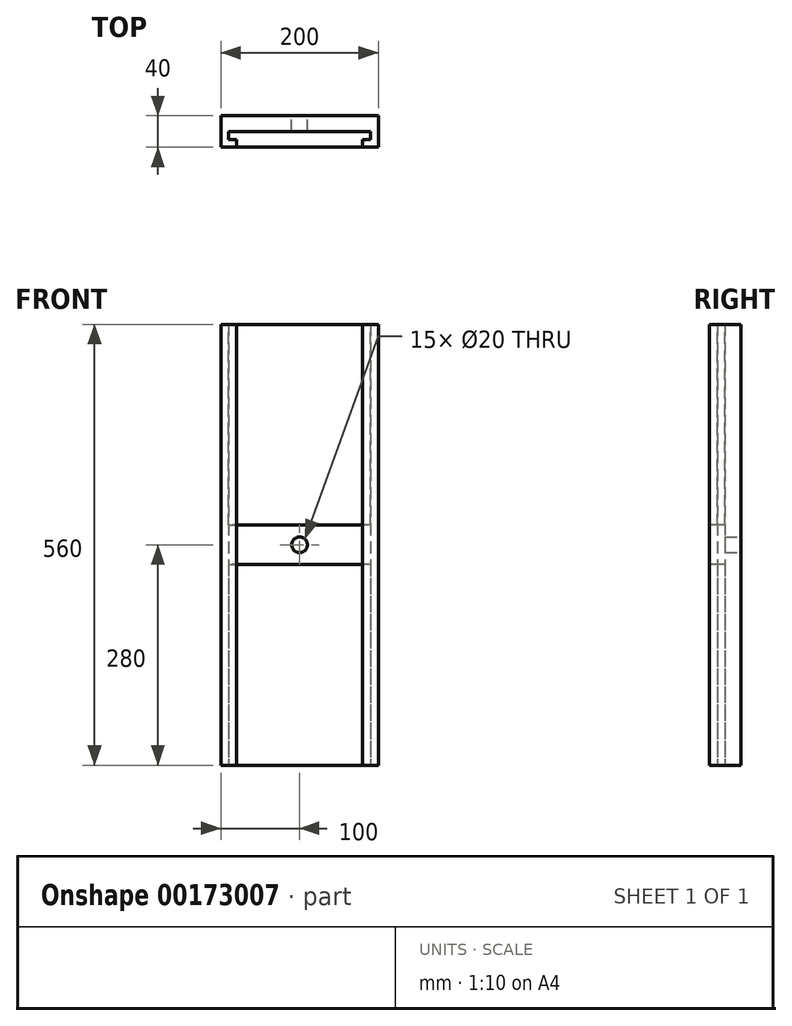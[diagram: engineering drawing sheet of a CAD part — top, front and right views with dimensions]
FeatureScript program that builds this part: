
annotation { "Feature Type Name" : "Feature", "Feature Type Description" : "" }
export const myFeature = defineFeature(function(context is Context, id is Id, definition is map)
    precondition{}
    {
        {
            var Q0;
            Q0=qCreatedBy(makeId("Top.planeOp"),FACE);
            var sketch = newSketch(context, id + "F0", { "sketchPlane" : qUnion([Q0])});
            skLineSegment(sketch, "E0", {"start": v(0, 20) * mm, "end": v(90, 20) * mm});
            skLineSegment(sketch, "E1", {"start": v(90, 20) * mm, "end": v(90, 10) * mm});
            skLineSegment(sketch, "E2", {"start": v(90, 10) * mm, "end": v(80, 10) * mm});
            skLineSegment(sketch, "E3", {"start": v(80, 10) * mm, "end": v(80, 0) * mm});
            skLineSegment(sketch, "E4", {"start": v(80, 0) * mm, "end": v(100, 0) * mm});
            skLineSegment(sketch, "E5", {"start": v(100, 0) * mm, "end": v(100, 40) * mm});
            skLineSegment(sketch, "E6", {"start": v(100, 40) * mm, "end": v(0, 40) * mm});
            skLineSegment(sketch, "E7", {"start": v(0, 40) * mm, "end": v(0, 0) * mm, "construction": true});
            skLineSegment(sketch, "E8.MirrorCS", {"start": v(-100, 40) * mm, "end": v(0, 40) * mm});
            skLineSegment(sketch, "E9.MirrorCS", {"start": v(0, 20) * mm, "end": v(-90, 20) * mm});
            skLineSegment(sketch, "E10.MirrorCS", {"start": v(-90, 20) * mm, "end": v(-90, 10) * mm});
            skLineSegment(sketch, "E11.MirrorCS", {"start": v(-90, 10) * mm, "end": v(-80, 10) * mm});
            skLineSegment(sketch, "E12.MirrorCS", {"start": v(-80, 10) * mm, "end": v(-80, 0) * mm});
            skLineSegment(sketch, "E13.MirrorCS", {"start": v(-80, 0) * mm, "end": v(-100, 0) * mm});
            skLineSegment(sketch, "E14.MirrorCS", {"start": v(-100, 0) * mm, "end": v(-100, 40) * mm});
            skSolve(sketch);
        }
        {
            var Q0;
            Q0 = qSketchRegion(id + "F0", true);
            extrude(context, id + "F1", {"entities" : qUnion([Q0]), "depth" : 280 * mm, "hasSecondDirection" : true, "secondDirectionOppositeDirection" : true, "secondDirectionDepth" : 280 * mm});
        }
        {
            var Q0;
            Q0=makeQuery(id+"F1.opExtrude","SWEPT_FACE",FACE,{"disambiguationData":[OSD([sQuery(id+"F0.wireOp",EDGE,"E6"),sQuery(id+"F0.wireOp",EDGE,"E8.MirrorCS")])]});
            var sketch = newSketch(context, id + "F2", { "sketchPlane" : qUnion([Q0])});
            skCircle(sketch, "E15", {"center": v(0, 0) * mm, "radius": 10 * mm});
            skSolve(sketch);
        }
        {
            var Q0;
            Q0 = qSketchRegion(id + "F2", true);
            extrude(context, id + "F3", {"entities" : qUnion([Q0]), "operationType" : NewBodyOperationType.REMOVE, "oppositeDirection" : true, "depth" : 20 * mm});
        }
        {
            var Q0;
            Q0=makeQuery(id+"F1.opExtrude","CAP_FACE",FACE,{"disambiguationData":[OSD([sQuery(id+"F0.wireOp",EDGE,"E0"),sQuery(id+"F0.wireOp",EDGE,"E1"),sQuery(id+"F0.wireOp",EDGE,"E2"),sQuery(id+"F0.wireOp",EDGE,"E3"),sQuery(id+"F0.wireOp",EDGE,"E4"),sQuery(id+"F0.wireOp",EDGE,"E5"),sQuery(id+"F0.wireOp",EDGE,"E6"),sQuery(id+"F0.wireOp",EDGE,"E8.MirrorCS"),sQuery(id+"F0.wireOp",EDGE,"E9.MirrorCS"),sQuery(id+"F0.wireOp",EDGE,"E10.MirrorCS"),sQuery(id+"F0.wireOp",EDGE,"E11.MirrorCS"),sQuery(id+"F0.wireOp",EDGE,"E12.MirrorCS"),sQuery(id+"F0.wireOp",EDGE,"E13.MirrorCS"),sQuery(id+"F0.wireOp",EDGE,"E14.MirrorCS")])],"isStart":false});
            var sketch = newSketch(context, id + "F4", { "sketchPlane" : qUnion([Q0])});
            skLineSegment(sketch, "E16", {"start": v(-90, 20) * mm, "end": v(-90, 10) * mm});
            skLineSegment(sketch, "E17", {"start": v(-90, 10) * mm, "end": v(-80, 10) * mm});
            skLineSegment(sketch, "E18", {"start": v(-80, 10) * mm, "end": v(-80, 0) * mm});
            skLineSegment(sketch, "E19", {"start": v(-80, 0) * mm, "end": v(80, 0) * mm});
            skLineSegment(sketch, "E20", {"start": v(80, 0) * mm, "end": v(80, 10) * mm});
            skLineSegment(sketch, "E21", {"start": v(80, 10) * mm, "end": v(90, 10) * mm});
            skLineSegment(sketch, "E22", {"start": v(90, 10) * mm, "end": v(90, 20) * mm});
            skLineSegment(sketch, "E23", {"start": v(90, 20) * mm, "end": v(-90, 20) * mm});
            skSolve(sketch);
        }
        {
            var Q0;
            Q0 = qSketchRegion(id + "F4", true);
            extrude(context, id + "F5", {"entities" : qUnion([Q0]), "oppositeDirection" : true, "depth" : 255 * mm});
        }
        {
            var Q0;
            Q0=makeQuery(id+"F1.opExtrude","CAP_FACE",FACE,{"disambiguationData":[OSD([sQuery(id+"F0.wireOp",EDGE,"E0"),sQuery(id+"F0.wireOp",EDGE,"E1"),sQuery(id+"F0.wireOp",EDGE,"E2"),sQuery(id+"F0.wireOp",EDGE,"E3"),sQuery(id+"F0.wireOp",EDGE,"E4"),sQuery(id+"F0.wireOp",EDGE,"E5"),sQuery(id+"F0.wireOp",EDGE,"E6"),sQuery(id+"F0.wireOp",EDGE,"E8.MirrorCS"),sQuery(id+"F0.wireOp",EDGE,"E9.MirrorCS"),sQuery(id+"F0.wireOp",EDGE,"E10.MirrorCS"),sQuery(id+"F0.wireOp",EDGE,"E11.MirrorCS"),sQuery(id+"F0.wireOp",EDGE,"E12.MirrorCS"),sQuery(id+"F0.wireOp",EDGE,"E13.MirrorCS"),sQuery(id+"F0.wireOp",EDGE,"E14.MirrorCS")])],"isStart":true});
            var sketch = newSketch(context, id + "F6", { "sketchPlane" : qUnion([Q0])});
            skLineSegment(sketch, "E24", {"start": v(-80, 0) * mm, "end": v(-80, -10) * mm});
            skLineSegment(sketch, "E25", {"start": v(-80, -10) * mm, "end": v(-90, -10) * mm});
            skLineSegment(sketch, "E26", {"start": v(-90, -10) * mm, "end": v(-90, -20) * mm});
            skLineSegment(sketch, "E27", {"start": v(-90, -20) * mm, "end": v(90, -20) * mm});
            skLineSegment(sketch, "E28", {"start": v(90, -20) * mm, "end": v(90, -10) * mm});
            skLineSegment(sketch, "E29", {"start": v(90, -10) * mm, "end": v(80, -10) * mm});
            skLineSegment(sketch, "E30", {"start": v(80, -10) * mm, "end": v(80, 0) * mm});
            skLineSegment(sketch, "E31", {"start": v(80, 0) * mm, "end": v(-80, 0) * mm});
            skSolve(sketch);
        }
        {
            var Q0;
            Q0 = qSketchRegion(id + "F6", true);
            extrude(context, id + "F7", {"entities" : qUnion([Q0]), "oppositeDirection" : true, "depth" : 255 * mm});
        }
    });
